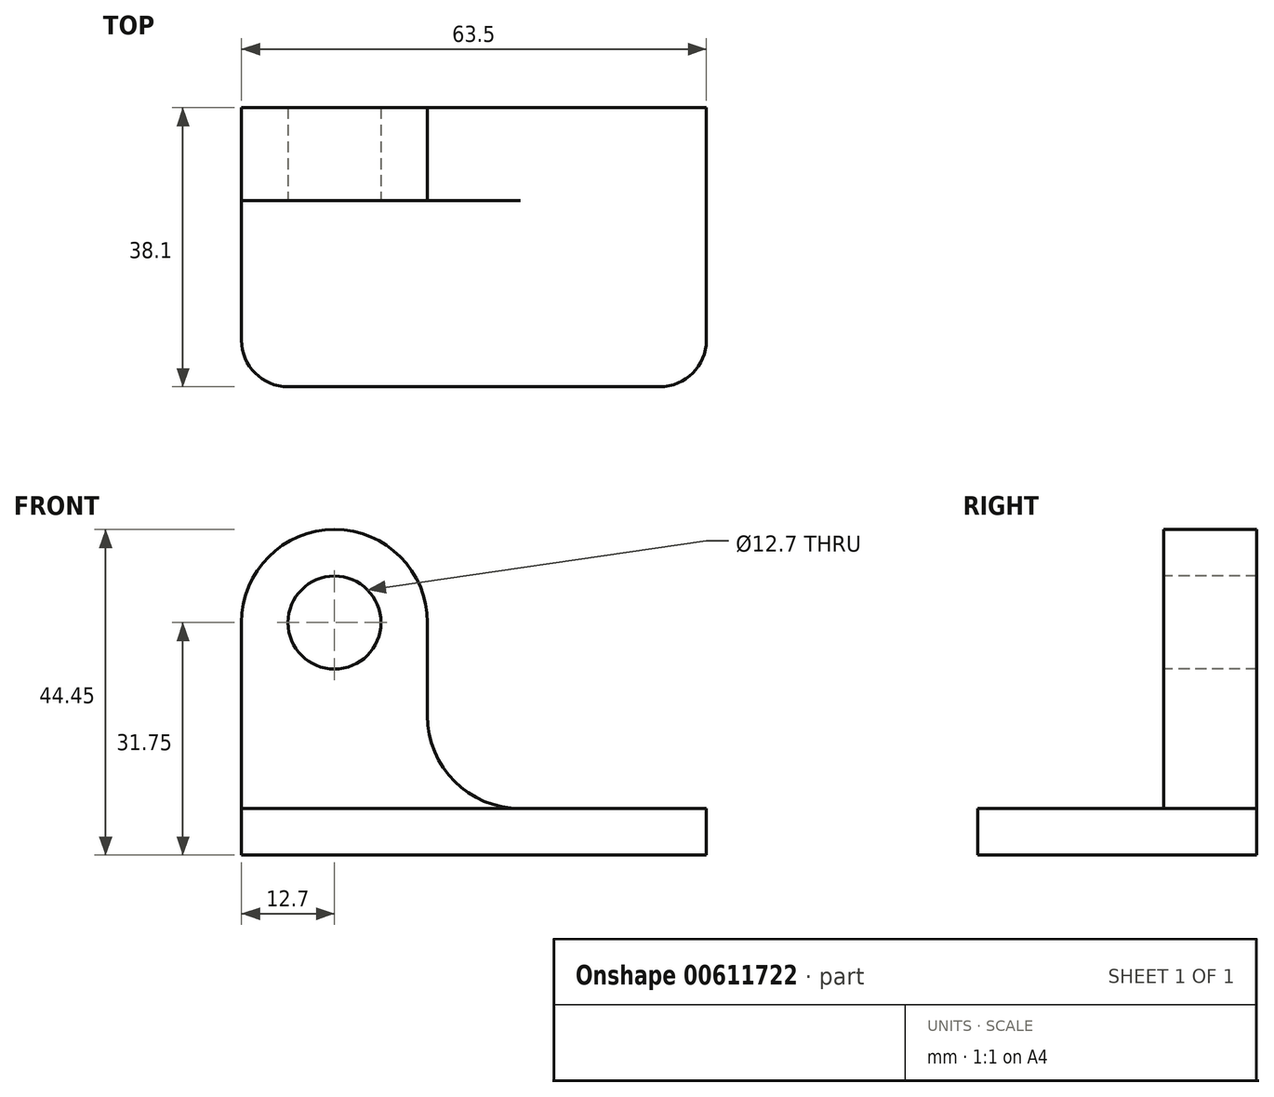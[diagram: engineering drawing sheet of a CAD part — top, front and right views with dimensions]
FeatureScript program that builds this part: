
annotation { "Feature Type Name" : "Feature", "Feature Type Description" : "" }
export const myFeature = defineFeature(function(context is Context, id is Id, definition is map)
    precondition{}
    {
        {
            var Q0;
            Q0=qCreatedBy(makeId("Front.planeOp"),FACE);
            var sketch = newSketch(context, id + "F0", { "sketchPlane" : qUnion([Q0])});
            skLineSegment(sketch, "E0.bottom", {"start": v(0, 0) * mm, "end": v(-63.5, 0) * mm});
            skLineSegment(sketch, "E0.top", {"start": v(0, 44.45) * mm, "end": v(-63.5, 44.45) * mm});
            skLineSegment(sketch, "E0.left", {"start": v(0, 0) * mm, "end": v(0, 44.45) * mm});
            skLineSegment(sketch, "E0.right", {"start": v(-63.5, 0) * mm, "end": v(-63.5, 44.45) * mm});
            skSolve(sketch);
        }
        {
            var Q0;
            Q0=makeQuery(id+"F0.imprint","IMPRINT",FACE,{"disambiguationData":[TD([[makeQuery(id+"F0.imprint","IMPRINT",EDGE,{"derivedFrom":sQuery(id+"F0.wireOp",EDGE,"E0.bottom")}),-1.0]])]});
            extrude(context, id + "F1", {"entities" : qUnion([Q0]), "depth" : 38.1 * mm, "offsetDistance" : 25.4 * mm});
        }
        {
            var Q0;
            Q0=makeQuery(id+"F1.opExtrude","SWEPT_FACE",FACE,{"disambiguationData":[OSD([sQuery(id+"F0.wireOp",EDGE,"E0.right")])]});
            var sketch = newSketch(context, id + "F2", { "sketchPlane" : qUnion([Q0])});
            skLineSegment(sketch, "E1", {"start": v(0, 6.35) * mm, "end": v(12.7, 6.35) * mm});
            skLineSegment(sketch, "E2", {"start": v(12.7, 6.35) * mm, "end": v(12.7, 0) * mm});
            skLineSegment(sketch, "E3", {"start": v(12.7, 6.35) * mm, "end": v(12.7, 44.45) * mm});
            skLineSegment(sketch, "E4", {"start": v(12.7, 6.35) * mm, "end": v(38.1, 6.35) * mm});
            skSolve(sketch);
        }
        {
            var Q0;
            {var subQ0=sQuery(id+"F2.wireOp",EDGE,"E3");Q0=makeQuery(id+"F2.imprint","IMPRINT",FACE,{"disambiguationData":[TD([[makeQuery(id+"F2.imprint","IMPRINT",EDGE,{"derivedFrom":subQ0}),-1.0]])]});}
            extrude(context, id + "F3", {"entities" : qUnion([Q0]), "operationType" : NewBodyOperationType.REMOVE, "endBound" : BoundingType.THROUGH_ALL, "oppositeDirection" : true, "depth" : 25.4 * mm, "offsetDistance" : 25.4 * mm});
        }
        {
            var Q0;
            Q0=makeQuery(id+"F3.boolean.opBoolean","COPY",FACE,{"derivedFrom":makeQuery(id+"F3.opExtrude","SWEPT_FACE",FACE,{"disambiguationData":[OSD([sQuery(id+"F2.wireOp",EDGE,"E3")])]})});
            var sketch = newSketch(context, id + "F4", { "sketchPlane" : qUnion([Q0])});
            skLineSegment(sketch, "E5", {"start": v(0, 6.35) * mm, "end": v(-25.4, 6.35) * mm});
            skLineSegment(sketch, "E6", {"start": v(-25.4, 6.35) * mm, "end": v(-25.4, 44.45) * mm});
            skSolve(sketch);
        }
        {
            var Q0;
            Q0=makeQuery(id+"F4.imprint","IMPRINT",FACE,{"disambiguationData":[TD([[makeQuery(id+"F4.imprint","IMPRINT",EDGE,{"derivedFrom":sQuery(id+"F4.wireOp",EDGE,"E5")}),-1.0]])]});
            extrude(context, id + "F5", {"entities" : qUnion([Q0]), "operationType" : NewBodyOperationType.REMOVE, "endBound" : BoundingType.THROUGH_ALL, "oppositeDirection" : true, "depth" : 25.4 * mm, "offsetDistance" : 25.4 * mm});
        }
        {
            var Q0;
            Q0=makeQuery(id+"F3.boolean.opBoolean","COPY",FACE,{"derivedFrom":makeQuery(id+"F3.opExtrude","SWEPT_FACE",FACE,{"disambiguationData":[OSD([sQuery(id+"F2.wireOp",EDGE,"E3")])]})});
            var sketch = newSketch(context, id + "F6", { "sketchPlane" : qUnion([Q0])});
            skLineSegment(sketch, "E7", {"start": v(-63.5, 44.45) * mm, "end": v(-63.5, 31.75) * mm});
            skLineSegment(sketch, "E8", {"start": v(-25.4, 6.35) * mm, "end": v(-38.1, 6.35) * mm});
            skLineSegment(sketch, "E9", {"start": v(-38.1, 44.45) * mm, "end": v(-38.1, 31.75) * mm});
            skArc(sketch, "E10", {"start": v(-38.1, 31.75) * mm, "mid": v(-50.8, 44.45) * mm, "end": v(-63.5, 31.75) * mm});
            skSolve(sketch);
        }
        {
            var Q0;
            {var subQ0=sQuery(id+"F6.wireOp",EDGE,"E9");Q0=makeQuery(id+"F6.imprint","IMPRINT",FACE,{"disambiguationData":[TD([[makeQuery(id+"F6.imprint","IMPRINT",EDGE,{"derivedFrom":subQ0}),-1.0]])]});}
            var Q1;
            {var subQ0=sQuery(id+"F6.wireOp",EDGE,"E7");Q1=makeQuery(id+"F6.imprint","IMPRINT",FACE,{"disambiguationData":[TD([[makeQuery(id+"F6.imprint","IMPRINT",EDGE,{"derivedFrom":subQ0}),-1.0]])]});}
            extrude(context, id + "F7", {"entities" : qUnion([Q0, Q1]), "operationType" : NewBodyOperationType.REMOVE, "endBound" : BoundingType.THROUGH_ALL, "oppositeDirection" : true, "depth" : 25.4 * mm, "offsetDistance" : 25.4 * mm});
        }
        {
            var Q0;
            Q0=makeQuery(id+"F3.boolean.opBoolean","COPY",FACE,{"derivedFrom":makeQuery(id+"F3.opExtrude","SWEPT_FACE",FACE,{"disambiguationData":[OSD([sQuery(id+"F2.wireOp",EDGE,"E3")])]})});
            var sketch = newSketch(context, id + "F8", { "sketchPlane" : qUnion([Q0])});
            skCircle(sketch, "E11", {"center": v(-50.8, 31.75) * mm, "radius": 6.35 * mm});
            skSolve(sketch);
        }
        {
            var Q0;
            Q0=makeQuery(id+"F8.imprint","IMPRINT",FACE,{"disambiguationData":[TD([[makeQuery(id+"F8.imprint","IMPRINT",EDGE,{"derivedFrom":sQuery(id+"F8.wireOp",EDGE,"E11")}),1.0]])]});
            extrude(context, id + "F9", {"entities" : qUnion([Q0]), "operationType" : NewBodyOperationType.REMOVE, "endBound" : BoundingType.THROUGH_ALL, "oppositeDirection" : true, "depth" : 25.4 * mm, "offsetDistance" : 25.4 * mm});
        }
        {
            var Q0;
            Q0=makeQuery(id+"F3.boolean.opBoolean","COPY",FACE,{"derivedFrom":makeQuery(id+"F3.opExtrude","SWEPT_FACE",FACE,{"disambiguationData":[OSD([sQuery(id+"F2.wireOp",EDGE,"E3")])]})});
            var sketch = newSketch(context, id + "F10", { "sketchPlane" : qUnion([Q0])});
            skLineSegment(sketch, "E12", {"start": v(-38.1, 31.75) * mm, "end": v(-38.1, 19.05) * mm});
            skLineSegment(sketch, "E13", {"start": v(-38.1, 19.05) * mm, "end": v(-25.4, 19.05) * mm});
            skSolve(sketch);
        }
        {
            var Q0;
            Q0=makeQuery(id+"F10.imprint","IMPRINT",FACE,{"disambiguationData":[TD([[makeQuery(id+"F10.imprint","IMPRINT",EDGE,{"derivedFrom":sQuery(id+"F10.wireOp",EDGE,"E12")}),1.0]])]});
            extrude(context, id + "F11", {"entities" : qUnion([Q0]), "operationType" : NewBodyOperationType.REMOVE, "endBound" : BoundingType.THROUGH_ALL, "oppositeDirection" : true, "depth" : 25.4 * mm, "offsetDistance" : 25.4 * mm});
        }
        {
            var Q0;
            Q0=makeQuery(id+"F3.boolean.opBoolean","COPY",FACE,{"derivedFrom":makeQuery(id+"F3.opExtrude","SWEPT_FACE",FACE,{"disambiguationData":[OSD([sQuery(id+"F2.wireOp",EDGE,"E3")])]})});
            var sketch = newSketch(context, id + "F12", { "sketchPlane" : qUnion([Q0])});
            skArc(sketch, "E14", {"start": v(-38.1, 19.05) * mm, "mid": v(-34.38, 10.07) * mm, "end": v(-25.4, 6.35) * mm});
            skSolve(sketch);
        }
        {
            var Q0;
            Q0=makeQuery(id+"F12.imprint","IMPRINT",FACE,{"disambiguationData":[TD([[makeQuery(id+"F12.imprint","IMPRINT",EDGE,{"derivedFrom":sQuery(id+"F12.wireOp",EDGE,"E14")}),1.0]])]});
            extrude(context, id + "F13", {"entities" : qUnion([Q0]), "operationType" : NewBodyOperationType.REMOVE, "endBound" : BoundingType.THROUGH_ALL, "oppositeDirection" : true, "depth" : 25.4 * mm, "offsetDistance" : 25.4 * mm});
        }
        {
            var Q0;
            Q0=makeQuery(id+"F5.boolean.opBoolean","MERGE",FACE,{"derivedFrom":[makeQuery(id+"F3.boolean.opBoolean","COPY",FACE,{"derivedFrom":makeQuery(id+"F3.opExtrude","SWEPT_FACE",FACE,{"disambiguationData":[OSD([sQuery(id+"F2.wireOp",EDGE,"E4")])]})}),makeQuery(id+"F5.opExtrude","SWEPT_FACE",FACE,{"disambiguationData":[OSD([sQuery(id+"F4.wireOp",EDGE,"E5")])]})]});
            var sketch = newSketch(context, id + "F14", { "sketchPlane" : qUnion([Q0])});
            skLineSegment(sketch, "E15", {"start": v(-63.5, -38.1) * mm, "end": v(-63.5, -31.75) * mm});
            skLineSegment(sketch, "E16", {"start": v(-63.5, -38.1) * mm, "end": v(-57.15, -38.1) * mm});
            skArc(sketch, "E17", {"start": v(-63.5, -31.75) * mm, "mid": v(-61.64, -36.24) * mm, "end": v(-57.15, -38.1) * mm});
            skSolve(sketch);
        }
        {
            var Q0;
            Q0=makeQuery(id+"F14.imprint","IMPRINT",FACE,{"disambiguationData":[TD([[makeQuery(id+"F14.imprint","IMPRINT",EDGE,{"derivedFrom":sQuery(id+"F14.wireOp",EDGE,"E15")}),1.0]])]});
            extrude(context, id + "F15", {"entities" : qUnion([Q0]), "operationType" : NewBodyOperationType.REMOVE, "oppositeDirection" : true, "depth" : 25.4 * mm, "offsetDistance" : 25.4 * mm});
        }
        {
            var Q0;
            Q0=makeQuery(id+"F5.boolean.opBoolean","MERGE",FACE,{"derivedFrom":[makeQuery(id+"F3.boolean.opBoolean","COPY",FACE,{"derivedFrom":makeQuery(id+"F3.opExtrude","SWEPT_FACE",FACE,{"disambiguationData":[OSD([sQuery(id+"F2.wireOp",EDGE,"E4")])]})}),makeQuery(id+"F5.opExtrude","SWEPT_FACE",FACE,{"disambiguationData":[OSD([sQuery(id+"F4.wireOp",EDGE,"E5")])]})]});
            var sketch = newSketch(context, id + "F16", { "sketchPlane" : qUnion([Q0])});
            skLineSegment(sketch, "E18", {"start": v(0, -38.1) * mm, "end": v(0, -31.75) * mm});
            skLineSegment(sketch, "E19", {"start": v(0, -38.1) * mm, "end": v(-6.35, -38.1) * mm});
            skArc(sketch, "E20", {"start": v(-6.35, -38.1) * mm, "mid": v(-1.86, -36.24) * mm, "end": v(0, -31.75) * mm});
            skSolve(sketch);
        }
        {
            var Q0;
            Q0=makeQuery(id+"F16.imprint","IMPRINT",FACE,{"disambiguationData":[TD([[makeQuery(id+"F16.imprint","IMPRINT",EDGE,{"derivedFrom":sQuery(id+"F16.wireOp",EDGE,"E18")}),-1.0]])]});
            extrude(context, id + "F17", {"entities" : qUnion([Q0]), "operationType" : NewBodyOperationType.REMOVE, "endBound" : BoundingType.THROUGH_ALL, "oppositeDirection" : true, "depth" : 25.4 * mm, "offsetDistance" : 25.4 * mm});
        }
    });
